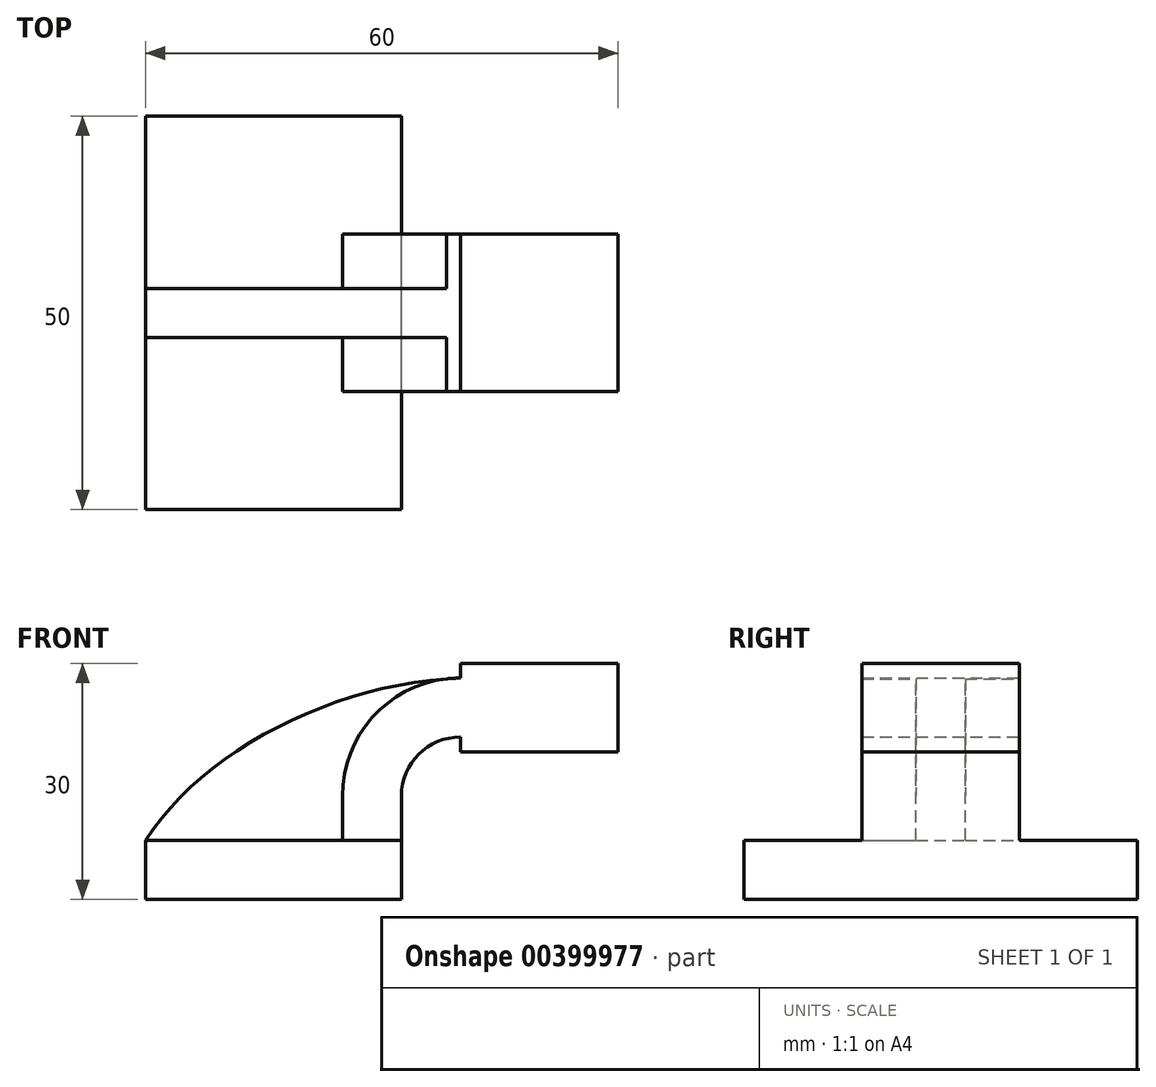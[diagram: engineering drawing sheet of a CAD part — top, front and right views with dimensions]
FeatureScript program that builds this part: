
annotation { "Feature Type Name" : "Feature", "Feature Type Description" : "" }
export const myFeature = defineFeature(function(context is Context, id is Id, definition is map)
    precondition{}
    {
        {
            var Q0;
            Q0=qCreatedBy(makeId("Front.planeOp"),FACE);
            var sketch = newSketch(context, id + "F0", { "sketchPlane" : qUnion([Q0])});
            skLineSegment(sketch, "E0.bottom", {"start": v(16.25, 3.75) * mm, "end": v(-16.25, 3.75) * mm});
            skLineSegment(sketch, "E0.top", {"start": v(16.25, -3.75) * mm, "end": v(-16.25, -3.75) * mm});
            skLineSegment(sketch, "E0.left", {"start": v(16.25, 3.75) * mm, "end": v(16.25, -3.75) * mm});
            skLineSegment(sketch, "E0.right", {"start": v(-16.25, 3.75) * mm, "end": v(-16.25, -3.75) * mm});
            skPoint(sketch, "E0.middle", {"position": v(0, 0) * mm});
            skLineSegment(sketch, "E1.bottom", {"start": v(43.75, 15) * mm, "end": v(23.75, 15) * mm});
            skLineSegment(sketch, "E1.top", {"start": v(43.75, 26.25) * mm, "end": v(23.75, 26.25) * mm});
            skLineSegment(sketch, "E1.left", {"start": v(43.75, 15) * mm, "end": v(43.75, 26.25) * mm});
            skLineSegment(sketch, "E1.right", {"start": v(23.75, 15) * mm, "end": v(23.75, 26.25) * mm});
            skPoint(sketch, "E1.middle", {"position": v(33.75, 20.63) * mm});
            skLineSegment(sketch, "E2", {"start": v(16.25, 3.75) * mm, "end": v(16.25, 9.38) * mm});
            skArc(sketch, "E3", {"start": v(16.25, 9.38) * mm, "mid": v(18.45, 14.68) * mm, "end": v(23.75, 16.88) * mm});
            skLineSegment(sketch, "E4", {"start": v(23.75, 16.88) * mm, "end": v(33.75, 16.88) * mm});
            skLineSegment(sketch, "E5.0", {"start": v(23.75, 24.38) * mm, "end": v(33.75, 24.38) * mm});
            skArc(sketch, "E5.1", {"start": v(8.75, 9.38) * mm, "mid": v(13.14, 19.99) * mm, "end": v(23.75, 24.38) * mm});
            skLineSegment(sketch, "E5.2", {"start": v(8.75, 3.75) * mm, "end": v(8.75, 9.38) * mm});
            skLineSegment(sketch, "E6", {"start": v(33.75, 15) * mm, "end": v(33.75, 26.25) * mm});
            skFitSpline(sketch, "E7", {"points": [v(-16.25, 3.75) * mm, v(23.75, 24.38) * mm], "startDerivative": vector(21.59, 34) * mm, "endDerivative": vector(48.43, 2.02) * mm});
            skSolve(sketch);
        }
        {
            var Q0;
            Q0=makeQuery(id+"F0.imprint","IMPRINT",FACE,{"disambiguationData":[TD([[makeQuery(id+"F0.imprint","IMPRINT",EDGE,{"derivedFrom":sQuery(id+"F0.wireOp",EDGE,"E0.top")}),-1.0]])]});
            extrude(context, id + "F1", {"entities" : qUnion([Q0]), "depth" : 50 * mm, "symmetric" : true});
        }
        {
            var Q0;
            {var subQ1=sQuery(id+"F0.wireOp",EDGE,"E2");Q0=makeQuery(id+"F0.imprint","IMPRINT",FACE,{"disambiguationData":[TD([[makeQuery(id+"F0.imprint","IMPRINT",EDGE,{"derivedFrom":subQ1}),1.0]])]});}
            var Q1;
            {var subQ0=sQuery(id+"F0.wireOp",EDGE,"E4");Q1=makeQuery(id+"F0.imprint","IMPRINT",FACE,{"disambiguationData":[TD([[makeQuery(id+"F0.imprint","IMPRINT",EDGE,{"derivedFrom":subQ0}),1.0]])]});}
            var Q2;
            {var subQ5=sQuery(id+"F0.wireOp",EDGE,"E4");Q2=makeQuery(id+"F0.imprint","IMPRINT",FACE,{"disambiguationData":[TD([[makeQuery(id+"F0.imprint","IMPRINT",EDGE,{"derivedFrom":subQ5}),-1.0]])]});}
            var Q3;
            {var subQ5=sQuery(id+"F0.wireOp",EDGE,"E5.0");Q3=makeQuery(id+"F0.imprint","IMPRINT",FACE,{"disambiguationData":[TD([[makeQuery(id+"F0.imprint","IMPRINT",EDGE,{"derivedFrom":subQ5}),1.0]])]});}
            var Q4;
            {var subQ0=sQuery(id+"F0.wireOp",EDGE,"E1.left");Q4=makeQuery(id+"F0.imprint","IMPRINT",FACE,{"disambiguationData":[TD([[makeQuery(id+"F0.imprint","IMPRINT",EDGE,{"derivedFrom":subQ0}),1.0]])]});}
            extrude(context, id + "F2", {"entities" : qUnion([Q0, Q1, Q2, Q3, Q4]), "operationType" : NewBodyOperationType.ADD, "depth" : 20 * mm, "symmetric" : true});
        }
        {
            var Q0;
            {var subQ3=sQuery(id+"F0.wireOp",EDGE,"E5.2");Q0=makeQuery(id+"F0.imprint","IMPRINT",FACE,{"disambiguationData":[TD([[makeQuery(id+"F0.imprint","IMPRINT",EDGE,{"derivedFrom":subQ3}),1.0]])]});}
            extrude(context, id + "F3", {"entities" : qUnion([Q0]), "operationType" : NewBodyOperationType.ADD, "depth" : 6.25 * mm, "symmetric" : true});
        }
    });
